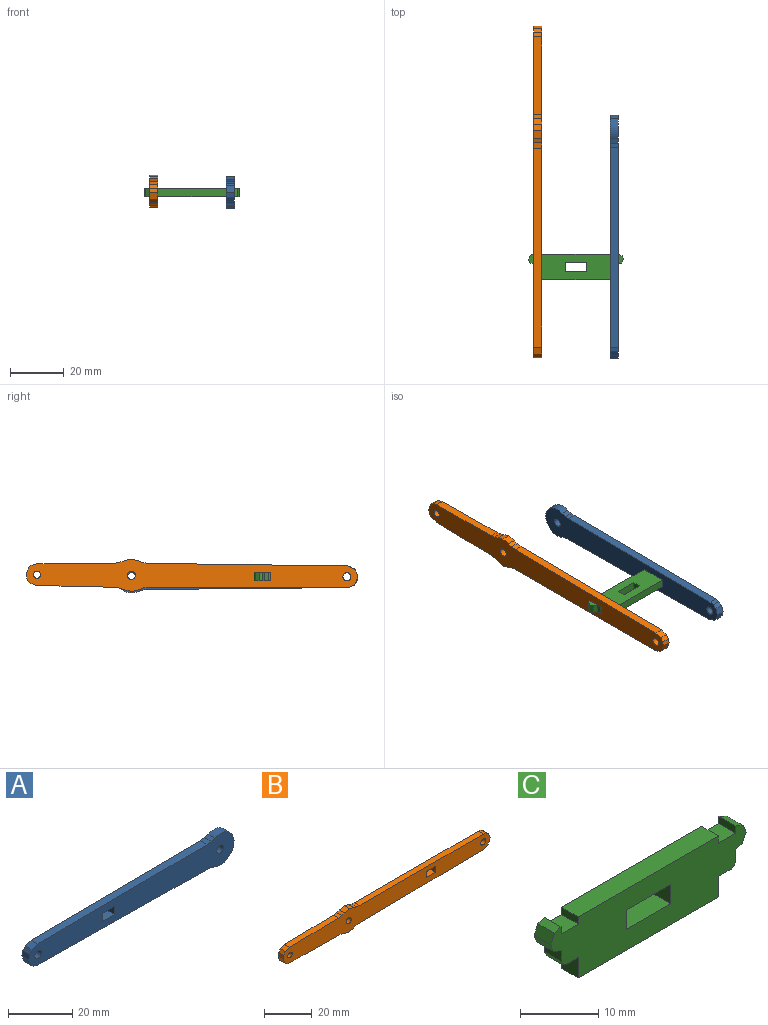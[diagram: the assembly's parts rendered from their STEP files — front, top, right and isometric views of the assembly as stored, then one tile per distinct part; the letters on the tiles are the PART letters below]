
ASSEMBLY  parts=3 mates=2
PART A: 23 faces, bbox 90.1x3x12 mm
  f0: plane 3x1.84mm, normal (-0.3,0,-0.95), area 5.8mm2, adj f1,f17,f20,f21
  f1: cylinder r=6mm len=7.21mm, axis (0,1,0), area 24mm2, adj f0,f2,f20,f21
  f2: cylinder r=6mm len=7.42mm, axis (0,1,0), area 24mm2, adj f1,f3,f20,f21
  f3: cylinder r=6mm len=7.21mm, axis (0,1,0), area 24mm2, adj f2,f4,f20,f21
  f4: plane 3x1.43mm, normal (-0.32,0,0.95), area 4.5mm2, adj f3,f5,f20,f21
  f5: plane 3x1.92mm, normal (-0.12,0,0.99), area 5.8mm2, adj f4,f6,f20,f21
  f6: plane 74.29x3mm, normal (-0.01,0,1), area 222.9mm2, adj f5,f7,f20,f21
  f7: plane 3x2.53mm, normal (-0.35,0,0.94), area 8.1mm2, adj f6,f8,f20,f21
  f8: plane 3x1.35mm, normal (-0.79,0,0.61), area 5.1mm2, adj f7,f9,f20,f21
  f9: plane 3x1.72mm, normal (-0.98,0,0.22), area 5.3mm2, adj f8,f10,f20,f21
  f10: plane 3x2.54mm, normal (-0.94,0,-0.34), area 8.1mm2, adj f9,f11,f20,f21
  f11: plane 3x1.34mm, normal (-0.62,0,-0.78), area 5.1mm2, adj f10,f12,f20,f21
  f12: plane 3x1.71mm, normal (-0.23,0,-0.97), area 5.3mm2, adj f11,f13,f20,f21
  f13: plane 74.29x3mm, normal (-0.01,0,-1), area 222.9mm2, adj f12,f17,f20,f21
  f14: plane 3.1x3mm, normal (1,0,0), area 9.3mm2, adj f15,f18,f20,f21
  f15: plane 5.37x3mm, normal (0,0,-1), area 16.1mm2, adj f14,f16,f20,f21
  f16: plane 3.1x3mm, normal (-1,0,0), area 9.3mm2, adj f15,f18,f20,f21
  f17: plane 3x1.51mm, normal (-0.1,0,-1), area 4.5mm2, adj f0,f13,f20,f21
  f18: plane 5.37x3mm, normal (0,0,1), area 16.1mm2, adj f14,f16,f20,f21
  f19: cylinder r=1.5mm len=3mm, axis (0,1,0), area 28.3mm2, adj f20,f21
  f20: plane 90.1x12mm, normal (0,-1,0), area 760.4mm2, adj f0,f1,f2,f3,f4,f5,f6,f7
  f21: plane 90.1x12mm, normal (0,1,0), area 760.4mm2, adj f0,f1,f2,f3,f4,f5,f6,f7
  f22: cylinder r=1.5mm len=3mm, axis (0,-1,0), area 28.3mm2, adj f20,f21
PART B: 41 faces, bbox 123.1x3x12 mm
  f0: plane 3.1x3mm, normal (-1,0,0), area 9.3mm2, adj f1,f35,f39,f40
  f1: plane 5.37x3mm, normal (0,0,1), area 16.1mm2, adj f0,f2,f39,f40
  f2: plane 3.1x3mm, normal (1,0,0), area 9.3mm2, adj f1,f35,f39,f40
  f3: plane 3x1.71mm, normal (-0.23,0,-0.97), area 5.3mm2, adj f4,f36,f39,f40
  f4: plane 3x0.1mm, normal (0,0,-1), area 0.3mm2, adj f3,f5,f39,f40
  f5: plane 28.82x3mm, normal (-0.01,0,-1), area 86.5mm2, adj f4,f6,f39,f40
  f6: plane 3x1.6mm, normal (-0.11,0,-0.99), area 4.8mm2, adj f5,f7,f39,f40
  f7: plane 3x1.93mm, normal (-0.33,0,-0.94), area 6.1mm2, adj f6,f8,f39,f40
  f8: plane 3x0.06mm, normal (-0.16,0,-0.99), area 0.2mm2, adj f7,f9,f39,f40
  f9: plane 3x2.39mm, normal (-0.27,0,-0.96), area 7.4mm2, adj f8,f10,f39,f40
  f10: plane 3.06x3mm, normal (0.2,0,-0.98), area 9.4mm2, adj f9,f11,f39,f40
  f11: plane 3x0.06mm, normal (0.74,0,0.67), area 0.3mm2, adj f10,f12,f39,f40
  f12: plane 3x1.51mm, normal (0.37,0,-0.93), area 4.9mm2, adj f11,f13,f39,f40
  f13: plane 3x2.05mm, normal (0.14,0,-0.99), area 6.2mm2, adj f12,f14,f39,f40
  f14: plane 73.74x3mm, normal (0.01,0,-1), area 221.2mm2, adj f13,f15,f39,f40
  f15: plane 3x2.54mm, normal (0.35,0,-0.94), area 8.1mm2, adj f14,f16,f39,f40
  f16: plane 3x1.35mm, normal (0.79,0,-0.61), area 5.1mm2, adj f15,f17,f39,f40
  f17: plane 3x1.72mm, normal (0.98,0,-0.21), area 5.3mm2, adj f16,f18,f39,f40
  f18: plane 3x2.54mm, normal (0.94,0,0.34), area 8.1mm2, adj f17,f19,f39,f40
  f19: plane 3x1.35mm, normal (0.61,0,0.79), area 5.1mm2, adj f18,f20,f39,f40
  f20: plane 3x1.72mm, normal (0.22,0,0.98), area 5.3mm2, adj f19,f21,f39,f40
  f21: plane 73.75x3mm, normal (0,0,1), area 221.2mm2, adj f20,f22,f39,f40
  f22: plane 3x1.62mm, normal (0.1,0,0.99), area 4.9mm2, adj f21,f23,f39,f40
  f23: plane 3x1.95mm, normal (0.33,0,0.94), area 6.2mm2, adj f22,f24,f39,f40
  f24: plane 3x2.39mm, normal (0.25,0,0.97), area 7.4mm2, adj f23,f25,f39,f40
  f25: plane 3.06x3mm, normal (-0.21,0,0.98), area 9.4mm2, adj f24,f26,f39,f40
  f26: plane 3x1.49mm, normal (-0.37,0,0.93), area 4.8mm2, adj f25,f27,f39,f40
  f27: plane 3x2.02mm, normal (-0.15,0,0.99), area 6.1mm2, adj f26,f28,f39,f40
  f28: plane 28.81x3mm, normal (-0.02,0,1), area 86.5mm2, adj f27,f29,f39,f40
  f29: plane 3x0.1mm, normal (0,0,1), area 0.3mm2, adj f28,f30,f39,f40
  f30: plane 3x2.51mm, normal (-0.36,0,0.93), area 8.1mm2, adj f29,f31,f39,f40
  f31: plane 3x1.35mm, normal (-0.8,0,0.6), area 5.1mm2, adj f30,f32,f39,f40
  f32: plane 3x1.71mm, normal (-0.98,0,0.21), area 5.3mm2, adj f31,f33,f39,f40
  f33: plane 3x2.53mm, normal (-0.94,0,-0.34), area 8.1mm2, adj f32,f36,f39,f40
  f34: cylinder r=1.5mm len=3mm, axis (0,1,0), area 28.3mm2, adj f39,f40
  f35: plane 5.37x3mm, normal (0,0,-1), area 16.1mm2, adj f0,f2,f39,f40
  f36: plane 3x1.33mm, normal (-0.62,0,-0.79), area 5.1mm2, adj f3,f33,f39,f40
  f37: cylinder r=1.5mm len=3mm, axis (0,1,0), area 28.3mm2, adj f39,f40
  f38: cylinder r=1.32mm len=3mm, axis (0,1,0), area 25mm2, adj f39,f40
  f39: plane 123.1x12.02mm, normal (0,-1,0), area 1011mm2, adj f0,f1,f2,f3,f4,f5,f6,f7
  f40: plane 123.1x12.02mm, normal (0,1,0), area 1011mm2, adj f0,f1,f2,f3,f4,f5,f6,f7
PART C: 32 faces, bbox 35.3x3x9.5 mm
  f0: plane 3x3mm, normal (1,0,0), area 9mm2, adj f1,f29,f30,f31
  f1: plane 8x3mm, normal (0,0,-1), area 24mm2, adj f0,f2,f30,f31
  f2: plane 3x3mm, normal (-1,0,0), area 9mm2, adj f1,f29,f30,f31
  f3: plane 3x1.18mm, normal (0.36,0,-0.93), area 3.8mm2, adj f4,f28,f30,f31
  f4: plane 3x1.42mm, normal (0.9,0,-0.44), area 4.7mm2, adj f3,f5,f30,f31
  f5: plane 3x1.25mm, normal (0.93,0,0.38), area 4mm2, adj f4,f6,f30,f31
  f6: plane 3x1.37mm, normal (0.42,0,0.91), area 4.5mm2, adj f5,f7,f30,f31
  f7: plane 3x1.12mm, normal (-1,0,0), area 3.4mm2, adj f6,f8,f30,f31
  f8: plane 3.1x3mm, normal (0,0,1), area 9.3mm2, adj f7,f9,f30,f31
  f9: plane 3x1.13mm, normal (1,0,0), area 3.4mm2, adj f8,f10,f30,f31
  f10: plane 25.3x3mm, normal (0,0,1), area 75.9mm2, adj f9,f11,f30,f31
  f11: plane 3x1.13mm, normal (-1,0,0), area 3.4mm2, adj f10,f12,f30,f31
  f12: plane 3.1x3mm, normal (0,0,1), area 9.3mm2, adj f11,f13,f30,f31
  f13: plane 3x1.11mm, normal (1,0,0), area 3.3mm2, adj f12,f14,f30,f31
  f14: plane 3x1.18mm, normal (-0.32,0,0.95), area 3.8mm2, adj f13,f15,f30,f31
  f15: plane 3x1.47mm, normal (-0.9,0,0.43), area 4.9mm2, adj f14,f16,f30,f31
  f16: plane 3x1.24mm, normal (-0.94,0,-0.34), area 3.9mm2, adj f15,f17,f30,f31
  f17: plane 3x1.43mm, normal (-0.41,0,-0.91), area 4.7mm2, adj f16,f18,f30,f31
  f18: plane 3x1.6mm, normal (-1,0,0), area 4.8mm2, adj f17,f19,f30,f31
  f19: plane 3x0.74mm, normal (-0.92,0,-0.39), area 2.4mm2, adj f18,f20,f30,f31
  f20: plane 3x0.79mm, normal (-0.29,0,-0.96), area 2.5mm2, adj f19,f21,f30,f31
  f21: plane 3x2mm, normal (0,0,-1), area 6mm2, adj f20,f22,f30,f31
  f22: plane 3.21x3mm, normal (-1,0,0), area 9.6mm2, adj f21,f23,f30,f31
  f23: plane 25.3x3mm, normal (0,0,-1), area 75.9mm2, adj f22,f24,f30,f31
  f24: plane 3.21x3mm, normal (1,0,0), area 9.6mm2, adj f23,f25,f30,f31
  f25: plane 3x2.31mm, normal (0,0,-1), area 6.9mm2, adj f24,f26,f30,f31
  f26: plane 3x0.49mm, normal (0.29,0,-0.96), area 1.5mm2, adj f25,f27,f30,f31
  f27: plane 3x0.63mm, normal (0.9,0,-0.44), area 2.1mm2, adj f26,f28,f30,f31
  f28: plane 3x1.8mm, normal (1,0,0), area 5.4mm2, adj f3,f27,f30,f31
  f29: plane 8x3mm, normal (0,0,1), area 24mm2, adj f0,f2,f30,f31
  f30: plane 35.25x9.54mm, normal (0,-1,0), area 259mm2, adj f0,f1,f2,f3,f4,f5,f6,f7
  f31: plane 35.25x9.54mm, normal (0,1,0), area 259mm2, adj f0,f1,f2,f3,f4,f5,f6,f7
PLACE A rot(axis=(-0.71,-0.71,0),180deg) t=(15.65,60.52,78.43)mm
PLACE B rot(axis=(-0.71,0.71,0),180deg) t=(-15.65,-36.83,90.13)mm
PLACE C rot(axis=(-1,0,0),90deg) t=(19.63,-42.58,0)mm
MATE fastened A.f22 <-> B.f34  axis (-1,0,0) through (12.65,-29.91,1.5)mm
MATE fastened A.f20 <-> C.f24  axis (-1,0,0) through (12.65,-1.81,1.5)mm
